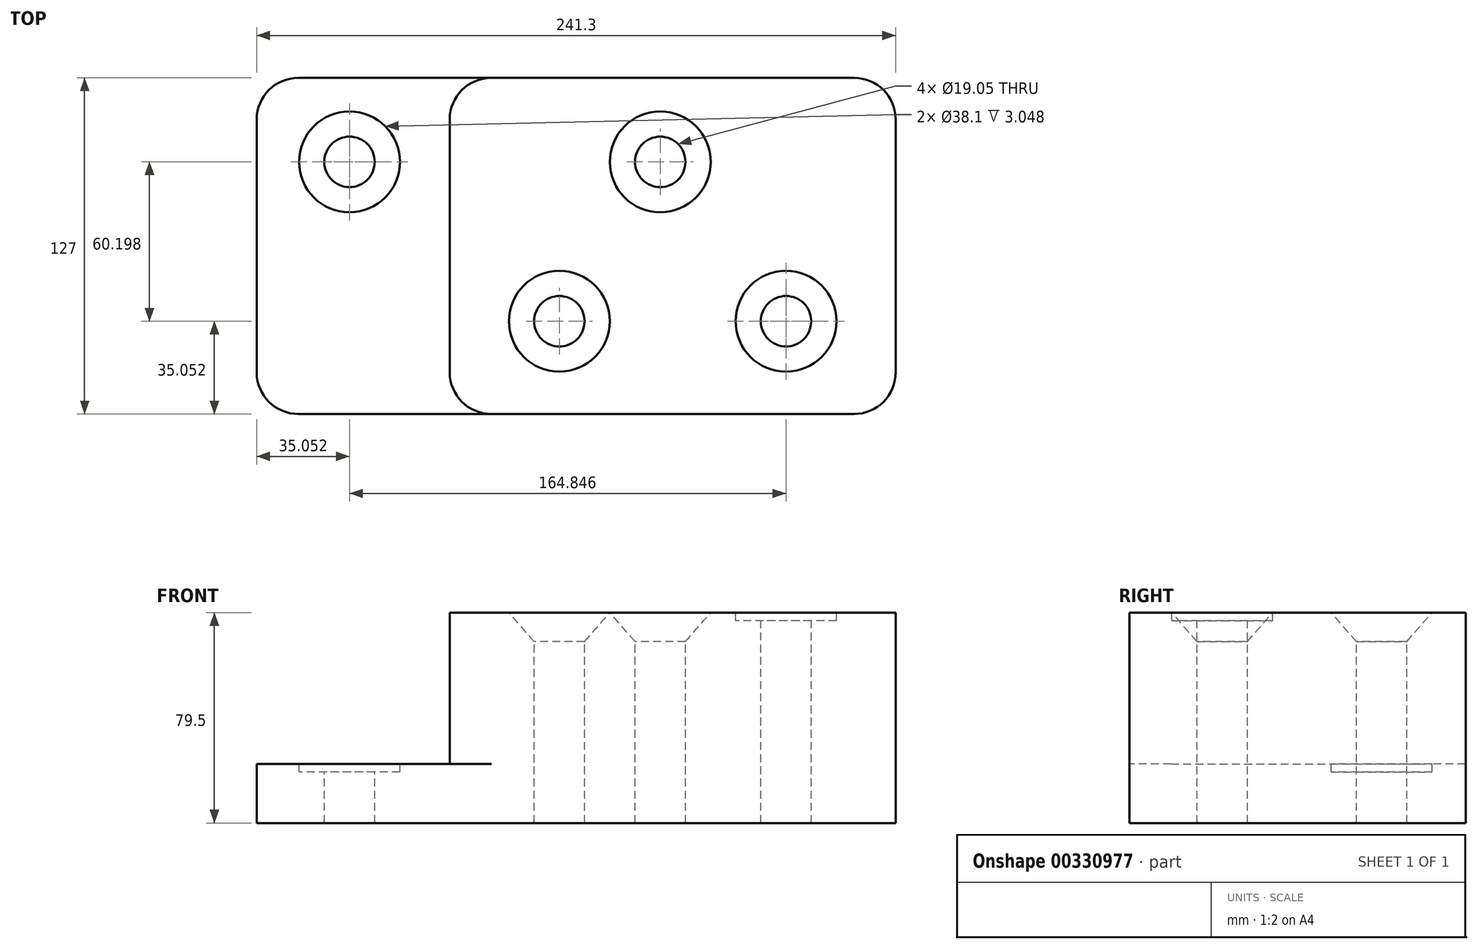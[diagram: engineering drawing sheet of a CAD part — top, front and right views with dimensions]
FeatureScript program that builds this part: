
annotation { "Feature Type Name" : "Feature", "Feature Type Description" : "" }
export const myFeature = defineFeature(function(context is Context, id is Id, definition is map)
    precondition{}
    {
        {
            var Q0;
            Q0=qCreatedBy(makeId("Top.planeOp"),FACE);
            var sketch = newSketch(context, id + "F0", { "sketchPlane" : qUnion([Q0])});
            skLineSegment(sketch, "E0.bottom", {"start": v(0, 0) * mm, "end": v(241.3, 0) * mm});
            skLineSegment(sketch, "E0.top", {"start": v(0, 127) * mm, "end": v(241.3, 127) * mm});
            skLineSegment(sketch, "E0.left", {"start": v(0, 0) * mm, "end": v(0, 127) * mm});
            skLineSegment(sketch, "E0.right", {"start": v(241.3, 0) * mm, "end": v(241.3, 127) * mm});
            skSolve(sketch);
        }
        {
            var Q0;
            Q0 = qSketchRegion(id + "F0", true);
            extrude(context, id + "F1", {"entities" : qUnion([Q0]), "depth" : 22.35 * mm});
        }
        {
            var Q0;
            Q0=makeQuery(id+"F1.opExtrude","CAP_FACE",FACE,{"disambiguationData":[OSD([sQuery(id+"F0.wireOp",EDGE,"E0.bottom"),sQuery(id+"F0.wireOp",EDGE,"E0.top"),sQuery(id+"F0.wireOp",EDGE,"E0.left"),sQuery(id+"F0.wireOp",EDGE,"E0.right")])],"isStart":false});
            var sketch = newSketch(context, id + "F2", { "sketchPlane" : qUnion([Q0])});
            skLineSegment(sketch, "E1.bottom", {"start": v(72.9, 127) * mm, "end": v(241.3, 127) * mm});
            skLineSegment(sketch, "E1.top", {"start": v(72.9, 0) * mm, "end": v(241.3, 0) * mm});
            skLineSegment(sketch, "E1.left", {"start": v(72.9, 127) * mm, "end": v(72.9, 0) * mm});
            skLineSegment(sketch, "E1.right", {"start": v(241.3, 127) * mm, "end": v(241.3, 0) * mm});
            skSolve(sketch);
        }
        {
            var Q0;
            Q0 = qSketchRegion(id + "F2", true);
            extrude(context, id + "F3", {"entities" : qUnion([Q0]), "operationType" : NewBodyOperationType.ADD, "depth" : 57.15 * mm});
        }
        {
            var Q0;
            Q0=makeQuery(id+"F1.opExtrude","CAP_FACE",FACE,{"disambiguationData":[OSD([sQuery(id+"F0.wireOp",EDGE,"E0.bottom"),sQuery(id+"F0.wireOp",EDGE,"E0.top"),sQuery(id+"F0.wireOp",EDGE,"E0.left"),sQuery(id+"F0.wireOp",EDGE,"E0.right")])],"isStart":false});
            var sketch = newSketch(context, id + "F4", { "sketchPlane" : qUnion([Q0])});
            skCircle(sketch, "E2", {"center": v(35.05, 95.25) * mm, "radius": 9.53 * mm});
            skCircle(sketch, "E3", {"center": v(35.05, 95.25) * mm, "radius": 19.05 * mm});
            skSolve(sketch);
        }
        {
            var Q0;
            Q0 = qSketchRegion(id + "F4", true);
            extrude(context, id + "F5", {"entities" : qUnion([Q0]), "operationType" : NewBodyOperationType.REMOVE, "oppositeDirection" : true, "depth" : 3.05 * mm});
        }
        {
            var Q0;
            Q0=makeQuery(id+"F5.boolean.opBoolean","SPLIT",FACE,{"disambiguationData":[TD([makeQuery(id+"F5.opExtrude","SWEPT_FACE",FACE,{"disambiguationData":[OSD([sQuery(id+"F4.wireOp",EDGE,"E2")])]})])],"derivedFrom":makeQuery(id+"F1.opExtrude","CAP_FACE",FACE,{"disambiguationData":[OSD([sQuery(id+"F0.wireOp",EDGE,"E0.bottom"),sQuery(id+"F0.wireOp",EDGE,"E0.top"),sQuery(id+"F0.wireOp",EDGE,"E0.left"),sQuery(id+"F0.wireOp",EDGE,"E0.right")])],"isStart":false})});
            extrude(context, id + "F6", {"entities" : qUnion([Q0]), "operationType" : NewBodyOperationType.REMOVE, "endBound" : BoundingType.THROUGH_ALL, "oppositeDirection" : true, "depth" : 25.4 * mm});
        }
        {
            var Q0;
            Q0=makeQuery(id+"F3.opExtrude","CAP_FACE",FACE,{"disambiguationData":[OSD([sQuery(id+"F2.wireOp",EDGE,"E1.bottom"),sQuery(id+"F2.wireOp",EDGE,"E1.top"),sQuery(id+"F2.wireOp",EDGE,"E1.left"),sQuery(id+"F2.wireOp",EDGE,"E1.right")])],"isStart":false});
            var sketch = newSketch(context, id + "F7", { "sketchPlane" : qUnion([Q0])});
            skCircle(sketch, "E4", {"center": v(199.9, 35.05) * mm, "radius": 9.53 * mm});
            skCircle(sketch, "E5", {"center": v(199.9, 35.05) * mm, "radius": 19.05 * mm});
            skSolve(sketch);
        }
        {
            var Q0;
            Q0 = qSketchRegion(id + "F7", true);
            extrude(context, id + "F8", {"entities" : qUnion([Q0]), "operationType" : NewBodyOperationType.REMOVE, "oppositeDirection" : true, "depth" : 3.05 * mm});
        }
        {
            var Q0;
            Q0=makeQuery(id+"F8.boolean.opBoolean","SPLIT",FACE,{"disambiguationData":[TD([makeQuery(id+"F8.opExtrude","SWEPT_FACE",FACE,{"disambiguationData":[OSD([sQuery(id+"F7.wireOp",EDGE,"E4")])]})])],"derivedFrom":makeQuery(id+"F3.opExtrude","CAP_FACE",FACE,{"disambiguationData":[OSD([sQuery(id+"F2.wireOp",EDGE,"E1.bottom"),sQuery(id+"F2.wireOp",EDGE,"E1.top"),sQuery(id+"F2.wireOp",EDGE,"E1.left"),sQuery(id+"F2.wireOp",EDGE,"E1.right")])],"isStart":false})});
            extrude(context, id + "F9", {"entities" : qUnion([Q0]), "operationType" : NewBodyOperationType.REMOVE, "endBound" : BoundingType.THROUGH_ALL, "oppositeDirection" : true, "depth" : 25.4 * mm});
        }
        {
            var Q0;
            {var subQ0=sQuery(id+"F2.wireOp",EDGE,"E1.bottom");var subQ1=sQuery(id+"F2.wireOp",EDGE,"E1.left");var subQ2=sQuery(id+"F2.wireOp",EDGE,"E1.top");var subQ3=sQuery(id+"F2.wireOp",EDGE,"E1.right");Q0=makeQuery(id+"F8.boolean.opBoolean","SPLIT",FACE,{"disambiguationData":[TD([makeQuery(id+"F1.opExtrude","SWEPT_FACE",FACE,{"disambiguationData":[OSD([sQuery(id+"F0.wireOp",EDGE,"E0.bottom")])]})])],"derivedFrom":makeQuery(id+"F3.opExtrude","CAP_FACE",FACE,{"disambiguationData":[OSD([subQ0,subQ2,subQ1,subQ3])],"isStart":false})});}
            var sketch = newSketch(context, id + "F10", { "sketchPlane" : qUnion([Q0])});
            skPoint(sketch, "E6", {"position": v(114.3, 35.05) * mm});
            skPoint(sketch, "E7", {"position": v(152.4, 95.25) * mm});
            skSolve(sketch);
        }
        {
            var Q0;
            Q0=sQuery(id+"F10.wireOp",VERTEX,"E6");
            var Q1;
            Q1=sQuery(id+"F10.wireOp",VERTEX,"E7");
            var Q2;
            Q2=makeQuery(id+"F1.opExtrude","SWEPT_BODY",BODY,{"disambiguationData":[OSD([sQuery(id+"F0.wireOp",EDGE,"E0.bottom"),sQuery(id+"F0.wireOp",EDGE,"E0.top"),sQuery(id+"F0.wireOp",EDGE,"E0.left"),sQuery(id+"F0.wireOp",EDGE,"E0.right")])]});
            hole(context, id + "F11", {"style" : HoleStyle.C_SINK, "endStyle" : HoleEndStyle.THROUGH, "holeDiameter" : 19.05 * mm, "cSinkDiameter" : 38.1 * mm, "cSinkAngle" : 82 * degree, "tappedDepth" : 12.7 * mm, "tapClearance" : 3, "locations" : qUnion([Q0, Q1]), "scope" : qUnion([Q2])});
        }
        {
            var Q0;
            Q0=makeQuery(id+"F1.opExtrude","SWEPT_EDGE",EDGE,{"disambiguationData":[OSD([sQuery(id+"F0.wireOp",EDGE,"E0.top"),sQuery(id+"F0.wireOp",EDGE,"E0.left")])]});
            var Q1;
            Q1=makeQuery(id+"F1.opExtrude","SWEPT_EDGE",EDGE,{"disambiguationData":[OSD([sQuery(id+"F0.wireOp",EDGE,"E0.bottom"),sQuery(id+"F0.wireOp",EDGE,"E0.left")])]});
            var Q2;
            Q2=makeQuery(id+"F3.opExtrude","SWEPT_EDGE",EDGE,{"disambiguationData":[OSD([sQuery(id+"F0.wireOp",EDGE,"E0.bottom"),sQuery(id+"F2.wireOp",EDGE,"E1.top"),sQuery(id+"F2.wireOp",EDGE,"E1.left")])]});
            var Q3;
            Q3=makeQuery(id+"F3.opExtrude","SWEPT_EDGE",EDGE,{"disambiguationData":[OSD([sQuery(id+"F0.wireOp",EDGE,"E0.top"),sQuery(id+"F2.wireOp",EDGE,"E1.bottom"),sQuery(id+"F2.wireOp",EDGE,"E1.left")])]});
            var Q4;
            Q4=makeQuery(id+"F3.boolean.opBoolean","MERGE",EDGE,{"derivedFrom":[makeQuery(id+"F1.opExtrude","SWEPT_EDGE",EDGE,{"disambiguationData":[OSD([sQuery(id+"F0.wireOp",EDGE,"E0.bottom"),sQuery(id+"F0.wireOp",EDGE,"E0.right")])]}),makeQuery(id+"F3.opExtrude","SWEPT_EDGE",EDGE,{"disambiguationData":[OSD([sQuery(id+"F2.wireOp",EDGE,"E1.top"),sQuery(id+"F2.wireOp",EDGE,"E1.right")])]})]});
            var Q5;
            Q5=makeQuery(id+"F3.boolean.opBoolean","MERGE",EDGE,{"derivedFrom":[makeQuery(id+"F1.opExtrude","SWEPT_EDGE",EDGE,{"disambiguationData":[OSD([sQuery(id+"F0.wireOp",EDGE,"E0.top"),sQuery(id+"F0.wireOp",EDGE,"E0.right")])]}),makeQuery(id+"F3.opExtrude","SWEPT_EDGE",EDGE,{"disambiguationData":[OSD([sQuery(id+"F2.wireOp",EDGE,"E1.bottom"),sQuery(id+"F2.wireOp",EDGE,"E1.right")])]})]});
            fillet(context, id + "F12", {"entities" : qUnion([Q0, Q1, Q2, Q3, Q4, Q5]), "radius" : 15.75 * mm, "tangentPropagation" : true, "allowEdgeOverflow" : false});
        }
    });
